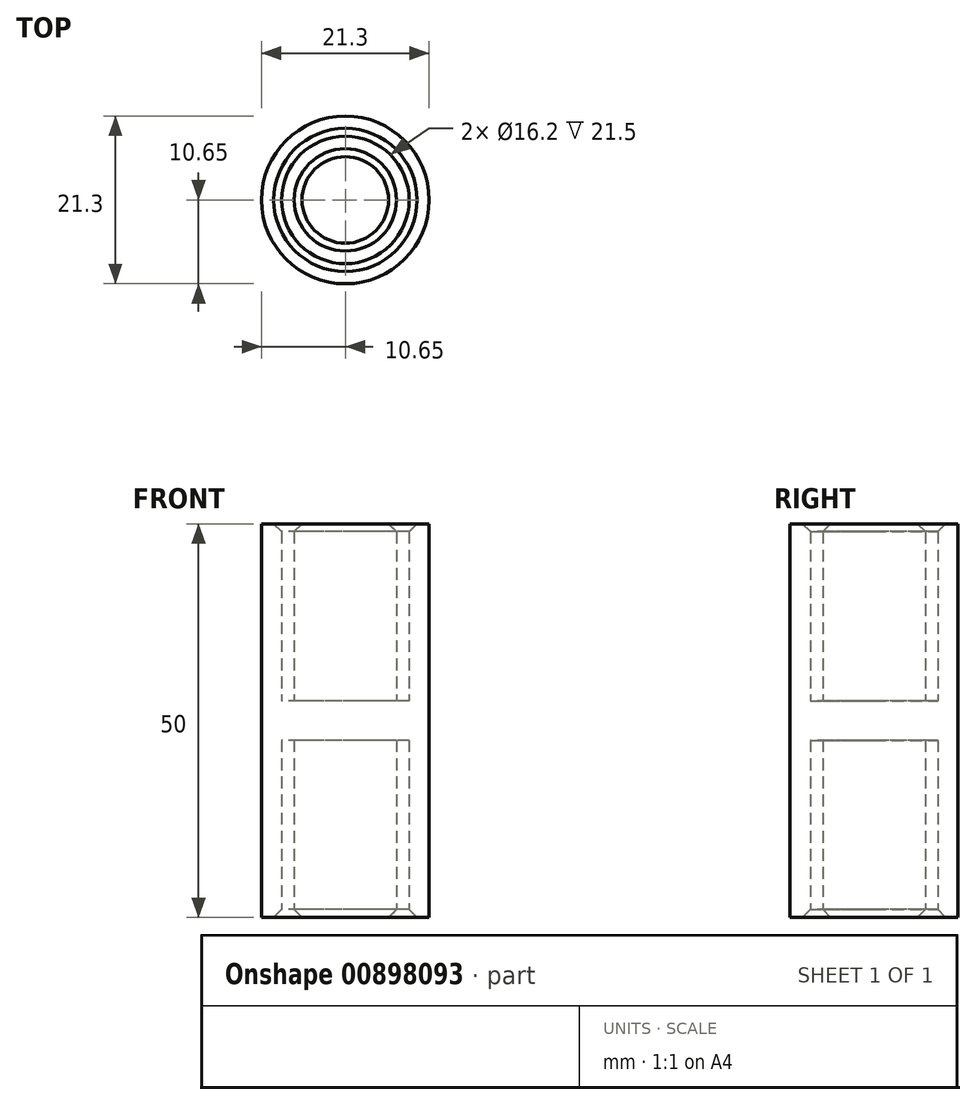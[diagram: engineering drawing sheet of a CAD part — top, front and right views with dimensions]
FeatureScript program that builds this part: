
annotation { "Feature Type Name" : "Feature", "Feature Type Description" : "" }
export const myFeature = defineFeature(function(context is Context, id is Id, definition is map)
    precondition{}
    {
        {
            var Q0;
            Q0=qCreatedBy(makeId("Top.planeOp"),FACE);
            var sketch = newSketch(context, id + "F0", { "sketchPlane" : qUnion([Q0])});
            skCircle(sketch, "E0", {"center": v(0, 0) * mm, "radius": 6.5 * mm});
            skCircle(sketch, "E1", {"center": v(0, 0) * mm, "radius": 8.1 * mm});
            skCircle(sketch, "E2", {"center": v(0, 0) * mm, "radius": 10.65 * mm});
            skSolve(sketch);
        }
        {
            var Q0;
            Q0 = qSketchRegion(id + "F0", true);
            extrude(context, id + "F1", {"entities" : qUnion([Q0]), "endBound" : BoundingType.SYMMETRIC, "depth" : 50 * mm, "offsetDistance" : 25 * mm});
        }
        {
            var Q0;
            Q0=makeQuery(id+"F0.imprint","IMPRINT",FACE,{"disambiguationData":[TD([[makeQuery(id+"F0.imprint","IMPRINT",EDGE,{"derivedFrom":sQuery(id+"F0.wireOp",EDGE,"E0")}),-1.0]])]});
            extrude(context, id + "F2", {"entities" : qUnion([Q0]), "operationType" : NewBodyOperationType.ADD, "endBound" : BoundingType.SYMMETRIC, "depth" : 5 * mm, "offsetDistance" : 25 * mm});
        }
        {
            var Q0;
            Q0=makeQuery(id+"F0.imprint","IMPRINT",FACE,{"disambiguationData":[TD([[makeQuery(id+"F0.imprint","IMPRINT",EDGE,{"derivedFrom":sQuery(id+"F0.wireOp",EDGE,"E0")}),1.0]])]});
            extrude(context, id + "F3", {"entities" : qUnion([Q0]), "operationType" : NewBodyOperationType.ADD, "endBound" : BoundingType.SYMMETRIC, "depth" : 50 * mm, "offsetDistance" : 25 * mm});
        }
        {
            var Q0;
            Q0=makeQuery(id+"F1.opExtrude","CAP_EDGE",EDGE,{"disambiguationData":[OSD([sQuery(id+"F0.wireOp",EDGE,"E1")])],"isStart":true});
            var Q1;
            Q1=makeQuery(id+"F3.opExtrude","CAP_FACE",FACE,{"disambiguationData":[OSD([sQuery(id+"F0.wireOp",EDGE,"E0")])],"isStart":true});
            var Q2;
            Q2=makeQuery(id+"F1.opExtrude","CAP_EDGE",EDGE,{"disambiguationData":[OSD([sQuery(id+"F0.wireOp",EDGE,"E1")])],"isStart":false});
            var Q3;
            Q3=makeQuery(id+"F3.opExtrude","CAP_FACE",FACE,{"disambiguationData":[OSD([sQuery(id+"F0.wireOp",EDGE,"E0")])],"isStart":false});
            chamfer(context, id + "F4", {"entities" : qUnion([Q0, Q1, Q2, Q3]), "width" : 1 * mm, "tangentPropagation" : true});
        }
    });
